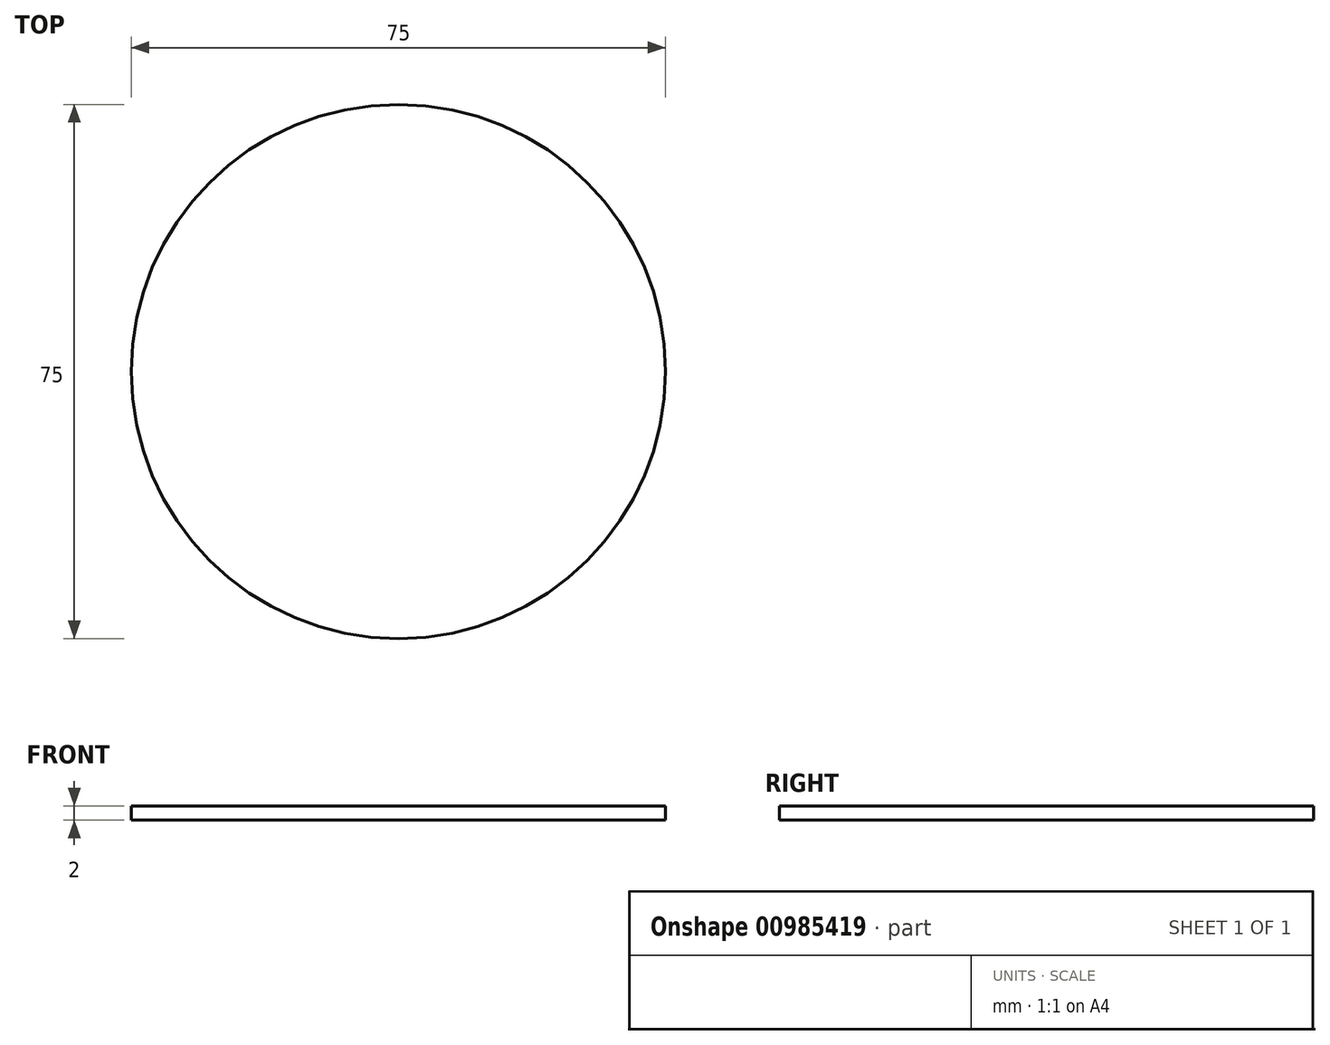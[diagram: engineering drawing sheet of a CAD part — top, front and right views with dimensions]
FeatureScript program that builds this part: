
annotation { "Feature Type Name" : "Feature", "Feature Type Description" : "" }
export const myFeature = defineFeature(function(context is Context, id is Id, definition is map)
    precondition{}
    {
        {
            var Q0;
            Q0=qCreatedBy(makeId("Top.planeOp"),FACE);
            var sketch = newSketch(context, id + "F0", { "sketchPlane" : qUnion([Q0])});
            skCircle(sketch, "E0", {"center": v(0, 0) * mm, "radius": 37.5 * mm});
            skSolve(sketch);
        }
        {
            var Q0;
            Q0=makeQuery(id+"F0.imprint","IMPRINT",FACE,{"disambiguationData":[TD([[makeQuery(id+"F0.imprint","IMPRINT",EDGE,{"derivedFrom":sQuery(id+"F0.wireOp",EDGE,"E0")}),1.0]])]});
            extrude(context, id + "F1", {"entities" : qUnion([Q0]), "depth" : 2 * mm, "offsetDistance" : 25 * mm});
        }
    });
